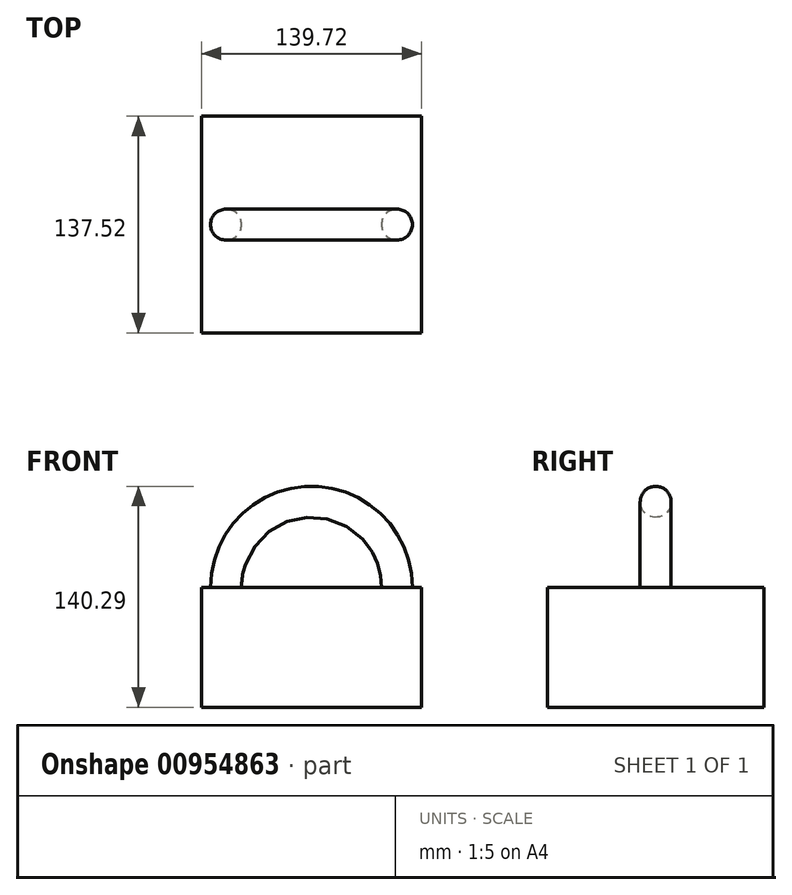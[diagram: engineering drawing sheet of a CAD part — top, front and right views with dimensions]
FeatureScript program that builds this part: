
annotation { "Feature Type Name" : "Feature", "Feature Type Description" : "" }
export const myFeature = defineFeature(function(context is Context, id is Id, definition is map)
    precondition{}
    {
        {
            var Q0;
            Q0=qCreatedBy(makeId("Top.planeOp"),FACE);
            var sketch = newSketch(context, id + "F0", { "sketchPlane" : qUnion([Q0])});
            skLineSegment(sketch, "E0.bottom", {"start": v(69.86, -68.76) * mm, "end": v(-69.86, -68.76) * mm});
            skLineSegment(sketch, "E0.top", {"start": v(69.86, 68.76) * mm, "end": v(-69.86, 68.76) * mm});
            skLineSegment(sketch, "E0.left", {"start": v(69.86, -68.76) * mm, "end": v(69.86, 68.76) * mm});
            skLineSegment(sketch, "E0.right", {"start": v(-69.86, -68.76) * mm, "end": v(-69.86, 68.76) * mm});
            skPoint(sketch, "E0.middle", {"position": v(0, 0) * mm});
            skLineSegment(sketch, "E1", {"start": v(0, 68.76) * mm, "end": v(0, -68.76) * mm});
            skSolve(sketch);
        }
        {
            var Q0;
            Q0=qCreatedBy(makeId("Top.planeOp"),FACE);
            var sketch = newSketch(context, id + "F1", { "sketchPlane" : qUnion([Q0])});
            skCircle(sketch, "E2", {"center": v(54.26, 0) * mm, "radius": 9.82 * mm});
            skSolve(sketch);
        }
        {
            var Q0;
            Q0=makeQuery(id+"F1.imprint","IMPRINT",FACE,{"disambiguationData":[TD([[makeQuery(id+"F1.imprint","IMPRINT",EDGE,{"derivedFrom":sQuery(id+"F1.wireOp",EDGE,"E2")}),1.0]])]});
            var Q1;
            Q1=sQuery(id+"F0.wireOp",EDGE,"E1");
            revolve(context, id + "F2", {"entities" : qUnion([Q0]), "axis" : qUnion([Q1]), "revolveType" : RevolveType.ONE_DIRECTION, "angle" : 180 * degree});
        }
        {
            var Q0;
            {var subQ0=sQuery(id+"F0.wireOp",EDGE,"E0.right");Q0=makeQuery(id+"F0.imprint","IMPRINT",FACE,{"disambiguationData":[TD([[makeQuery(id+"F0.imprint","IMPRINT",EDGE,{"derivedFrom":subQ0}),-1.0]])]});}
            var Q1;
            {var subQ0=sQuery(id+"F0.wireOp",EDGE,"E0.left");Q1=makeQuery(id+"F0.imprint","IMPRINT",FACE,{"disambiguationData":[TD([[makeQuery(id+"F0.imprint","IMPRINT",EDGE,{"derivedFrom":subQ0}),1.0]])]});}
            extrude(context, id + "F3", {"entities" : qUnion([Q0, Q1]), "operationType" : NewBodyOperationType.ADD, "depth" : -76.2 * mm, "offsetDistance" : 25.4 * mm});
        }
    });
